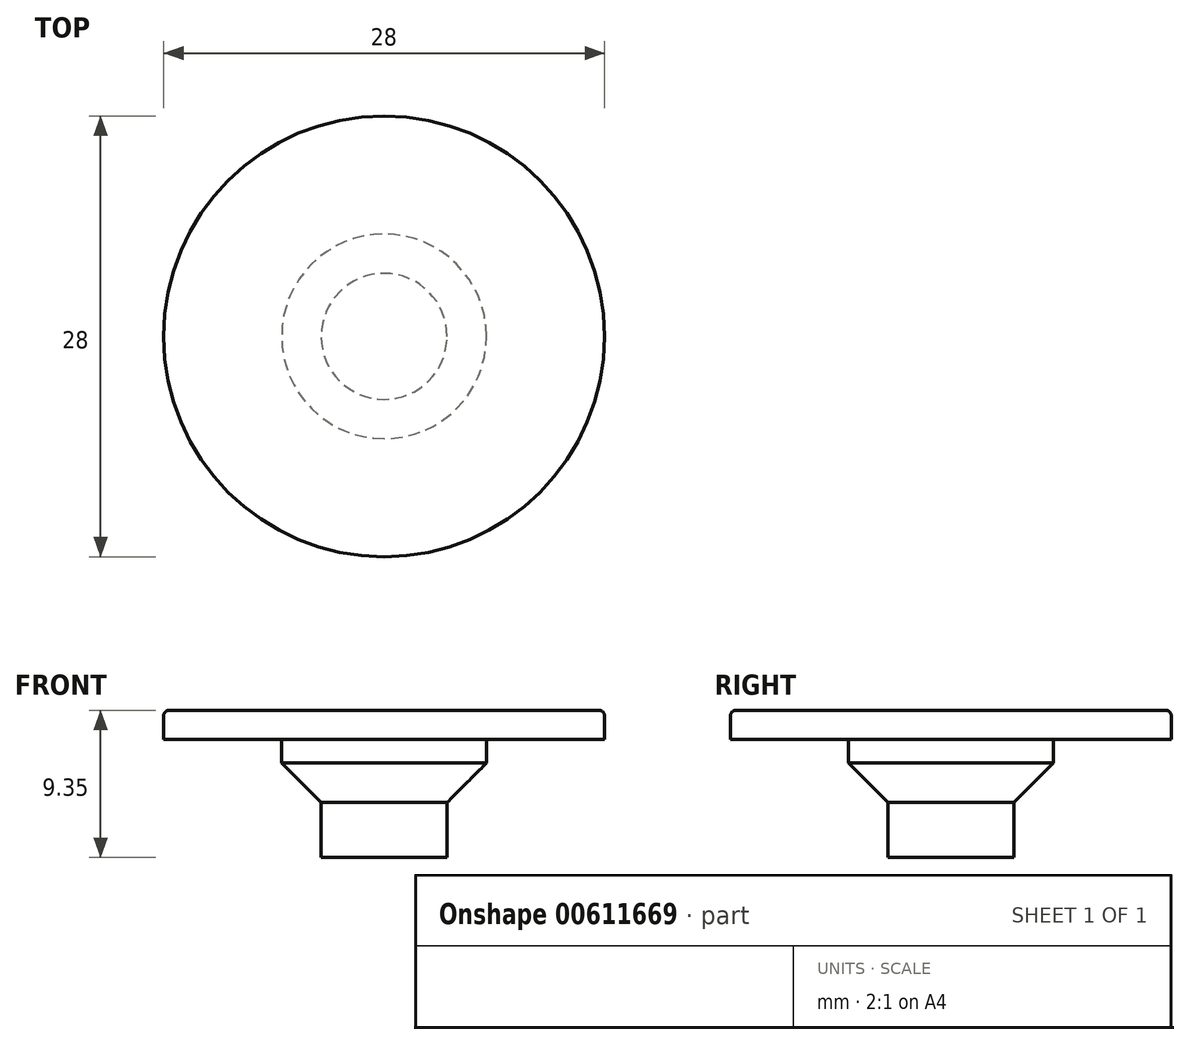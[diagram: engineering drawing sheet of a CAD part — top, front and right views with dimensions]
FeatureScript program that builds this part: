
annotation { "Feature Type Name" : "Feature", "Feature Type Description" : "" }
export const myFeature = defineFeature(function(context is Context, id is Id, definition is map)
    precondition{}
    {
        {
            var Q0;
            Q0=qCreatedBy(makeId("Front.planeOp"),FACE);
            var sketch = newSketch(context, id + "F0", { "sketchPlane" : qUnion([Q0])});
            skLineSegment(sketch, "E0", {"start": v(4, 0.5) * mm, "end": v(6.5, 3) * mm});
            skLineSegment(sketch, "E1", {"start": v(6.5, 4.5) * mm, "end": v(14, 4.5) * mm});
            skLineSegment(sketch, "E2", {"start": v(14, 4.5) * mm, "end": v(14, 6) * mm});
            skArc(sketch, "E3", {"start": v(13.65, 6.35) * mm, "mid": v(13.9, 6.25) * mm, "end": v(14, 6) * mm});
            skLineSegment(sketch, "E4", {"start": v(0, -3) * mm, "end": v(4, -3) * mm});
            skLineSegment(sketch, "E5", {"start": v(4, 0.5) * mm, "end": v(4, -3) * mm});
            skLineSegment(sketch, "E6", {"start": v(0, 6.35) * mm, "end": v(0, -3) * mm});
            skLineSegment(sketch, "E7", {"start": v(0, 6.35) * mm, "end": v(13.65, 6.35) * mm});
            skLineSegment(sketch, "E8", {"start": v(6.5, 4.5) * mm, "end": v(6.5, 3) * mm});
            skSolve(sketch);
        }
        {
            var Q0;
            Q0=makeQuery(id+"F0.imprint","IMPRINT",FACE,{"disambiguationData":[TD([[makeQuery(id+"F0.imprint","IMPRINT",EDGE,{"derivedFrom":sQuery(id+"F0.wireOp",EDGE,"E0")}),1.0]])]});
            var Q1;
            Q1=sQuery(id+"F0.wireOp",EDGE,"E6");
            revolve(context, id + "F1", {"entities" : qUnion([Q0]), "axis" : qUnion([Q1]), "revolveType" : RevolveType.FULL});
        }
    });
